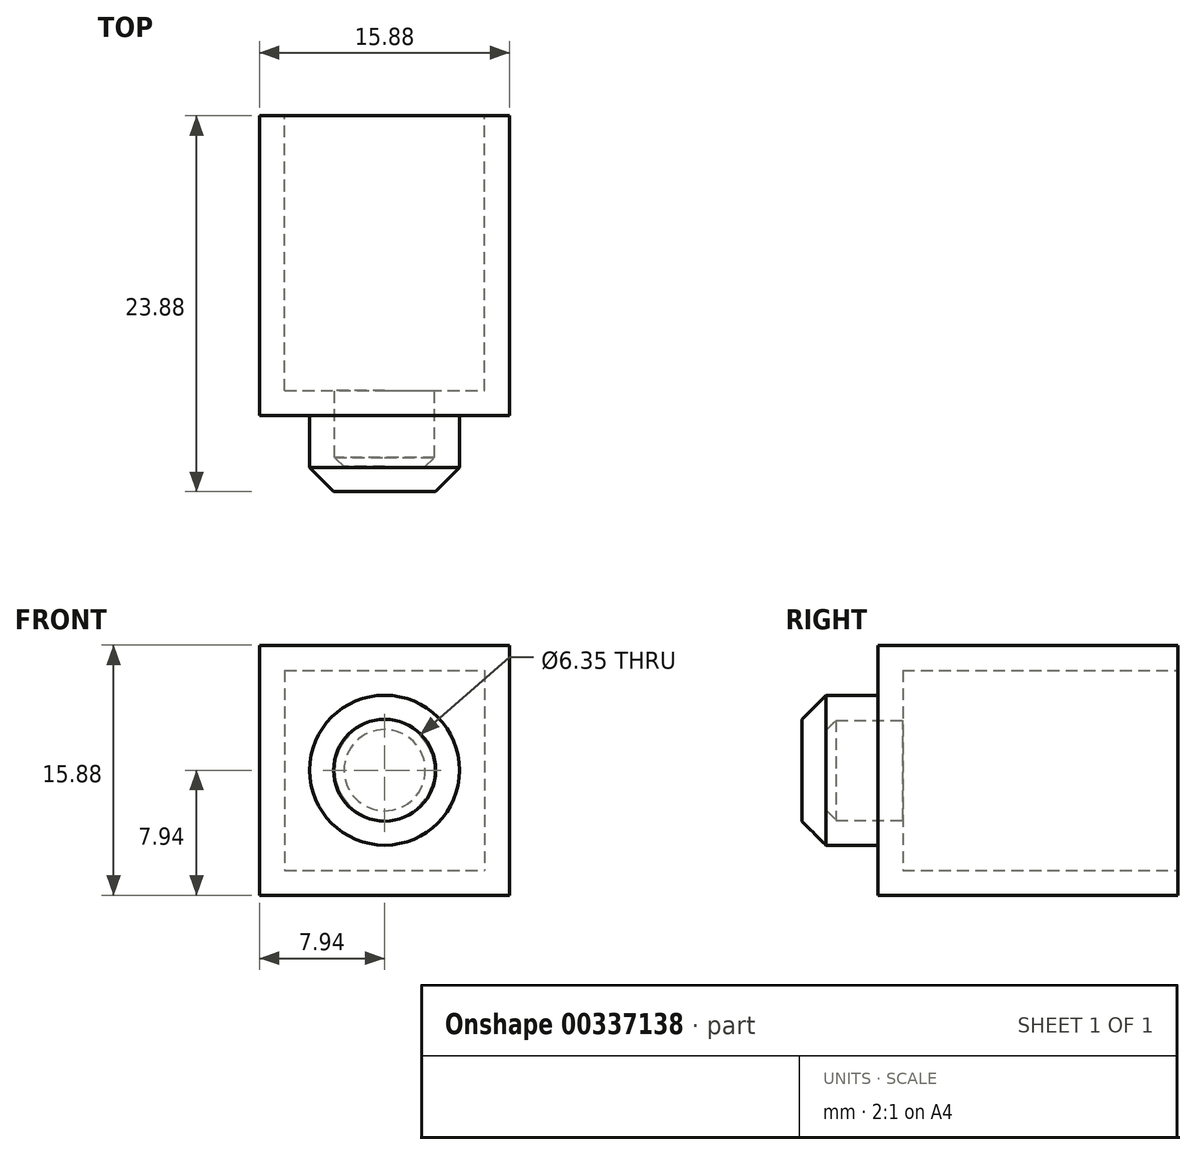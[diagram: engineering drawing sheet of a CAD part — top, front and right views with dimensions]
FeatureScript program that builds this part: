
annotation { "Feature Type Name" : "Feature", "Feature Type Description" : "" }
export const myFeature = defineFeature(function(context is Context, id is Id, definition is map)
    precondition{}
    {
        {
            var Q0;
            Q0=qCreatedBy(makeId("Front.planeOp"),FACE);
            var sketch = newSketch(context, id + "F0", { "sketchPlane" : qUnion([Q0])});
            skLineSegment(sketch, "E0.bottom", {"start": v(-7.94, 7.94) * mm, "end": v(7.94, 7.94) * mm});
            skLineSegment(sketch, "E0.top", {"start": v(-7.94, -7.94) * mm, "end": v(7.94, -7.94) * mm});
            skLineSegment(sketch, "E0.left", {"start": v(-7.94, 7.94) * mm, "end": v(-7.94, -7.94) * mm});
            skLineSegment(sketch, "E0.right", {"start": v(7.94, 7.94) * mm, "end": v(7.94, -7.94) * mm});
            skPoint(sketch, "E0.middle", {"position": v(0, 0) * mm});
            skSolve(sketch);
        }
        {
            var Q0;
            Q0=qSketchRegion(id+"F0",true);
            extrude(context, id + "F1", {"entities" : qUnion([Q0]), "depth" : 19.05 * mm});
        }
        {
            var Q0;
            Q0=makeQuery(id+"F1.opExtrude","CAP_FACE",FACE,{"disambiguationData":[OSD([sQuery(id+"F0.wireOp",EDGE,"E0.bottom"),sQuery(id+"F0.wireOp",EDGE,"E0.top"),sQuery(id+"F0.wireOp",EDGE,"E0.left"),sQuery(id+"F0.wireOp",EDGE,"E0.right")])],"isStart":false});
            var sketch = newSketch(context, id + "F2", { "sketchPlane" : qUnion([Q0])});
            skCircle(sketch, "E1", {"center": v(0, 0) * mm, "radius": 4.76 * mm});
            skSolve(sketch);
        }
        {
            var Q0;
            Q0=qSketchRegion(id+"F2",true);
            extrude(context, id + "F3", {"entities" : qUnion([Q0]), "operationType" : NewBodyOperationType.ADD, "depth" : 4.83 * mm});
        }
        {
            var Q0;
            Q0=makeQuery(id+"F3.opExtrude","CAP_FACE",FACE,{"disambiguationData":[OSD([sQuery(id+"F2.wireOp",EDGE,"E1")])],"isStart":false});
            var Q1;
            Q1=makeQuery(id+"FCYf6MEHPLtkZFw_1.1.F3.opExtrude","CAP_FACE",FACE,{"disambiguationData":[OSD([sQuery(id+"F2.wireOp",EDGE,"E1")])],"isStart":false});
            var Q2;
            Q2=makeQuery(id+"FCYf6MEHPLtkZFw_1.0_1.F3.opExtrude","CAP_FACE",FACE,{"disambiguationData":[OSD([sQuery(id+"F2.wireOp",EDGE,"E1")])],"isStart":false});
            var Q3;
            Q3=makeQuery(id+"FCYf6MEHPLtkZFw_1.1_1.F3.opExtrude","CAP_FACE",FACE,{"disambiguationData":[OSD([sQuery(id+"F2.wireOp",EDGE,"E1")])],"isStart":false});
            var Q4;
            Q4=makeQuery(id+"FCYf6MEHPLtkZFw_1.0_2.F3.opExtrude","CAP_FACE",FACE,{"disambiguationData":[OSD([sQuery(id+"F2.wireOp",EDGE,"E1")])],"isStart":false});
            var Q5;
            Q5=makeQuery(id+"FCYf6MEHPLtkZFw_1.1_2.F3.opExtrude","CAP_FACE",FACE,{"disambiguationData":[OSD([sQuery(id+"F2.wireOp",EDGE,"E1")])],"isStart":false});
            var Q6;
            Q6=makeQuery(id+"FCYf6MEHPLtkZFw_1.0_3.F3.opExtrude","CAP_FACE",FACE,{"disambiguationData":[OSD([sQuery(id+"F2.wireOp",EDGE,"E1")])],"isStart":false});
            var Q7;
            Q7=makeQuery(id+"FCYf6MEHPLtkZFw_1.1_3.F3.opExtrude","CAP_FACE",FACE,{"disambiguationData":[OSD([sQuery(id+"F2.wireOp",EDGE,"E1")])],"isStart":false});
            chamfer(context, id + "F4", {"entities" : qUnion([Q0, Q1, Q2, Q3, Q4, Q5, Q6, Q7]), "width" : 1.52 * mm, "tangentPropagation" : true});
        }
        {
            var Q0;
            Q0=makeQuery(id+"F1.opExtrude","CAP_FACE",FACE,{"disambiguationData":[OSD([sQuery(id+"F0.wireOp",EDGE,"E0.bottom"),sQuery(id+"F0.wireOp",EDGE,"E0.top"),sQuery(id+"F0.wireOp",EDGE,"E0.left"),sQuery(id+"F0.wireOp",EDGE,"E0.right")])],"isStart":true});
            shell(context, id + "F5", {"entities" : qUnion([Q0]), "thickness" : 1.59 * mm});
        }
    });
